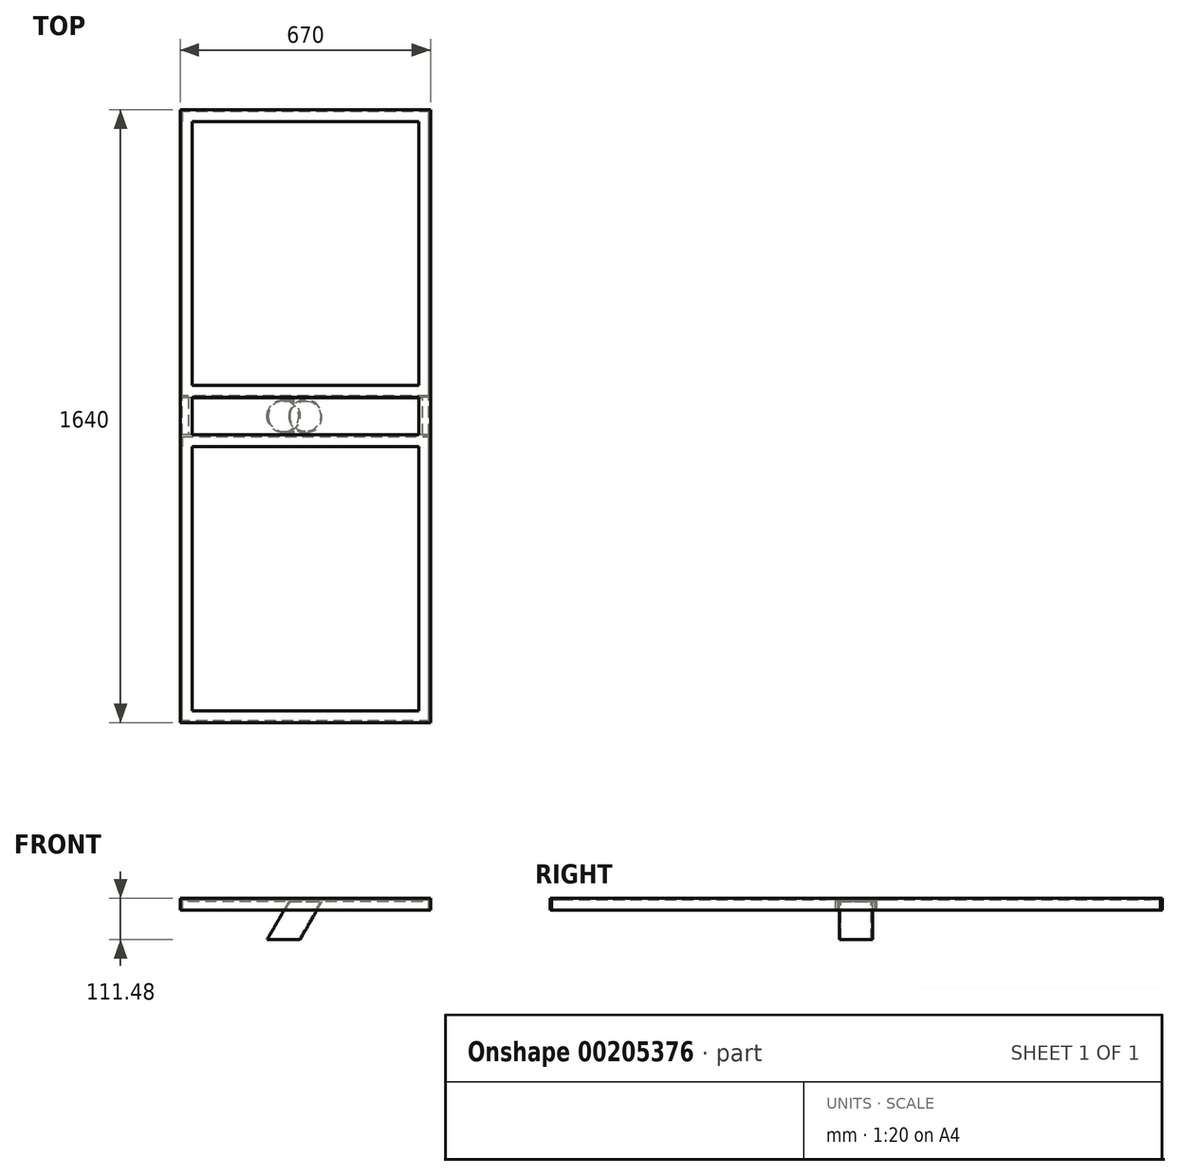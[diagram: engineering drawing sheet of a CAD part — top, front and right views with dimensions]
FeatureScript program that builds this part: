
annotation { "Feature Type Name" : "Feature", "Feature Type Description" : "" }
export const myFeature = defineFeature(function(context is Context, id is Id, definition is map)
    precondition{}
    {
        {
            var Q0;
            Q0=qCreatedBy(makeId("Right.planeOp"),FACE);
            var sketch = newSketch(context, id + "F0", { "sketchPlane" : qUnion([Q0])});
            skLineSegment(sketch, "E0", {"start": v(-385, -21.75) * mm, "end": v(-385, 10) * mm});
            skLineSegment(sketch, "E1", {"start": v(-385, 10) * mm, "end": v(-353.25, 10) * mm});
            skLineSegment(sketch, "E2", {"start": v(-353.25, 10) * mm, "end": v(-353.25, 5.24) * mm});
            skLineSegment(sketch, "E3", {"start": v(-353.25, 5.24) * mm, "end": v(-380.24, 5.24) * mm});
            skLineSegment(sketch, "E4", {"start": v(-380.24, 5.24) * mm, "end": v(-380.24, -21.75) * mm});
            skLineSegment(sketch, "E5", {"start": v(-380.24, -21.75) * mm, "end": v(-385, -21.75) * mm});
            skLineSegment(sketch, "E6.MirrorCS", {"start": v(353.25, 10) * mm, "end": v(353.25, 5.24) * mm});
            skLineSegment(sketch, "E7.MirrorCS", {"start": v(380.24, -21.75) * mm, "end": v(385, -21.75) * mm});
            skLineSegment(sketch, "E8.MirrorCS", {"start": v(385, -21.75) * mm, "end": v(385, 10) * mm});
            skLineSegment(sketch, "E9.MirrorCS", {"start": v(385, 10) * mm, "end": v(353.25, 10) * mm});
            skLineSegment(sketch, "E10.MirrorCS", {"start": v(380.24, 5.24) * mm, "end": v(380.24, -21.75) * mm});
            skLineSegment(sketch, "E11.MirrorCS", {"start": v(353.25, 5.24) * mm, "end": v(380.24, 5.24) * mm});
            skSolve(sketch);
        }
        {
            var Q0;
            Q0 = qSketchRegion(id + "F0", true);
            extrude(context, id + "F1", {"entities" : qUnion([Q0]), "endBound" : BoundingType.SYMMETRIC, "depth" : 670 * mm});
        }
        {
            var Q0;
            Q0=qCreatedBy(makeId("Right.planeOp"),FACE);
            var sketch = newSketch(context, id + "F2", { "sketchPlane" : qUnion([Q0])});
            skLineSegment(sketch, "E12", {"start": v(384.61, 0) * mm, "end": v(484.61, 0) * mm});
            skLineSegment(sketch, "E13", {"start": v(434.61, 0) * mm, "end": v(434.61, 59.63) * mm, "construction": true});
            skLineSegment(sketch, "E14.bottom", {"start": v(484.61, 0) * mm, "end": v(384.5, 0) * mm});
            skLineSegment(sketch, "E14.top", {"start": v(484.61, 8.14) * mm, "end": v(384.5, 8.14) * mm});
            skLineSegment(sketch, "E14.left", {"start": v(484.61, 0) * mm, "end": v(484.61, 8.14) * mm});
            skLineSegment(sketch, "E14.right", {"start": v(384.5, 0) * mm, "end": v(384.5, 8.14) * mm});
            skPoint(sketch, "E15.start.orphan", {"position": v(384.61, -9.19) * mm});
            skSolve(sketch);
        }
        {
            var Q0;
            Q0=qCreatedBy(makeId("Front.planeOp"),FACE);
            cPlane(context, id + "F3", {"entities" : qUnion([Q0]), "cplaneType" : CPlaneType.OFFSET, "offset" : 385 * mm + 50 * mm, "oppositeDirection" : true, "width" : 150 * mm, "height" : 150 * mm});
        }
        {
            var Q0;
            Q0=makeQuery(id+"F1.opExtrude","SWEPT_BODY",BODY,{"disambiguationData":[OSD([sQuery(id+"F0.wireOp",EDGE,"E0"),sQuery(id+"F0.wireOp",EDGE,"E1"),sQuery(id+"F0.wireOp",EDGE,"E2"),sQuery(id+"F0.wireOp",EDGE,"E3"),sQuery(id+"F0.wireOp",EDGE,"E4"),sQuery(id+"F0.wireOp",EDGE,"E5")])]});
            var Q1;
            Q1=makeQuery(id+"F1.opExtrude","SWEPT_BODY",BODY,{"disambiguationData":[OSD([sQuery(id+"F0.wireOp",EDGE,"E6.MirrorCS"),sQuery(id+"F0.wireOp",EDGE,"E7.MirrorCS"),sQuery(id+"F0.wireOp",EDGE,"E10.MirrorCS"),sQuery(id+"F0.wireOp",EDGE,"E11.MirrorCS"),sQuery(id+"F0.wireOp",EDGE,"E9.MirrorCS"),sQuery(id+"F0.wireOp",EDGE,"E8.MirrorCS")])]});
            var Q2;
            Q2=qCreatedBy(id+"F3.planeOp",FACE);
            mirror(context, id + "F4", {"entities" : qUnion([Q0, Q1]), "mirrorPlane" : qUnion([Q2])});
        }
        {
            var Q0;
            Q0 = qSketchRegion(id + "F2", true);
            extrude(context, id + "F5", {"entities" : qUnion([Q0]), "operationType" : NewBodyOperationType.ADD, "endBound" : BoundingType.SYMMETRIC, "depth" : 628 * mm});
        }
        {
            var Q0;
            Q0=qCreatedBy(id+"F3.planeOp",FACE);
            var sketch = newSketch(context, id + "F6", { "sketchPlane" : qUnion([Q0])});
            skLineSegment(sketch, "E16", {"start": v(0, 0) * mm, "end": v(-58.59, -101.48) * mm});
            skSolve(sketch);
        }
        {
            var Q0;
            Q0=makeQuery(id+"F5.opExtrude","SWEPT_FACE",FACE,{"disambiguationData":[OSD([sQuery(id+"F2.wireOp",EDGE,"E14.bottom")])]});
            var sketch = newSketch(context, id + "F7", { "sketchPlane" : qUnion([Q0])});
            skCircle(sketch, "E17", {"center": v(0, -434.8) * mm, "radius": 44.12 * mm});
            skPoint(sketch, "E17.centerSnap0", {"position": v(314, -434.8) * mm});
            skCircle(sketch, "E18", {"center": v(0, -434.8) * mm, "radius": 41 * mm});
            skSolve(sketch);
        }
        {
            var Q0;
            Q0=makeQuery(id+"F7.imprint","IMPRINT",FACE,{"disambiguationData":[TD([[makeQuery(id+"F7.imprint","IMPRINT",EDGE,{"derivedFrom":sQuery(id+"F7.wireOp",EDGE,"E17")}),1.0]])]});
            var Q1;
            Q1=sQuery(id+"F6.wireOp",EDGE,"E16");
            sweep(context, id + "F8", {"operationType" : NewBodyOperationType.ADD, "profiles" : qUnion([Q0]), "path" : qUnion([Q1])});
        }
        {
            var Q0;
            Q0=qCreatedBy(id+"F3.planeOp",FACE);
            var sketch = newSketch(context, id + "F9", { "sketchPlane" : qUnion([Q0])});
            skLineSegment(sketch, "E19", {"start": v(0, 0) * mm, "end": v(330.24, 0) * mm, "construction": true});
            skLineSegment(sketch, "E20", {"start": v(330.24, 0) * mm, "end": v(330.24, 5.24) * mm});
            skLineSegment(sketch, "E21", {"start": v(330.24, 5.24) * mm, "end": v(303.25, 5.24) * mm});
            skLineSegment(sketch, "E22", {"start": v(303.25, 5.24) * mm, "end": v(303.25, 10) * mm});
            skLineSegment(sketch, "E23", {"start": v(303.25, 10) * mm, "end": v(335, 10) * mm});
            skLineSegment(sketch, "E24", {"start": v(335, 10) * mm, "end": v(335, -21.75) * mm});
            skLineSegment(sketch, "E25", {"start": v(335, -21.75) * mm, "end": v(330.24, -21.75) * mm});
            skLineSegment(sketch, "E26", {"start": v(330.24, -21.75) * mm, "end": v(330.24, 5.24) * mm});
            skLineSegment(sketch, "E27.MirrorCS", {"start": v(-330.24, 0) * mm, "end": v(-330.24, 5.24) * mm});
            skLineSegment(sketch, "E28.MirrorCS", {"start": v(-303.25, 5.24) * mm, "end": v(-303.25, 10) * mm});
            skLineSegment(sketch, "E29.MirrorCS", {"start": v(-335, -21.75) * mm, "end": v(-330.24, -21.75) * mm});
            skLineSegment(sketch, "E30.MirrorCS", {"start": v(-330.24, 5.24) * mm, "end": v(-303.25, 5.24) * mm});
            skLineSegment(sketch, "E31.MirrorCS", {"start": v(0, 0) * mm, "end": v(-330.24, 0) * mm, "construction": true});
            skLineSegment(sketch, "E32.MirrorCS", {"start": v(-303.25, 10) * mm, "end": v(-335, 10) * mm});
            skLineSegment(sketch, "E33.MirrorCS", {"start": v(-330.24, -21.75) * mm, "end": v(-330.24, 5.24) * mm});
            skLineSegment(sketch, "E34.MirrorCS", {"start": v(-335, 10) * mm, "end": v(-335, -21.75) * mm});
            skSolve(sketch);
        }
        {
            var Q0;
            {var subQ0=sQuery(id+"F9.wireOp",EDGE,"E21");Q0=makeQuery(id+"F9.imprint","IMPRINT",FACE,{"disambiguationData":[TD([[makeQuery(id+"F9.imprint","IMPRINT",EDGE,{"derivedFrom":subQ0}),-1.0]])]});}
            var Q1;
            Q1=makeQuery(id+"F9.imprint","IMPRINT",FACE,{"disambiguationData":[TD([[makeQuery(id+"F9.imprint","IMPRINT",EDGE,{"derivedFrom":sQuery(id+"F9.wireOp",EDGE,"E28.MirrorCS")}),1.0]])]});
            var Q2;
            Q2=sQuery(id+"F9.wireOp",EDGE,"E24");
            extrude(context, id + "F10", {"entities" : qUnion([Q0, Q1]), "operationType" : NewBodyOperationType.ADD, "surfaceEntities" : qUnion([Q2]), "endBound" : BoundingType.SYMMETRIC, "depth" : 1630 * mm});
        }
    });
